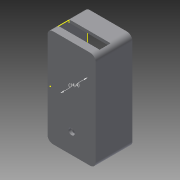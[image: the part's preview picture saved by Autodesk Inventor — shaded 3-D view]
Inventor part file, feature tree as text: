
AUTODESK INVENTOR PART (.ipt)
format: ipt  version: 2014 (Build 180170000, 170)  size: 256,512 bytes
history: native  units: mm
features: sketch x11, extrude x10, projected_geometry x3, fillet x2, chamfer x1
ambient origin geometry x8: Origin, YZ Plane, XZ Plane, XY Plane, X Axis, Y Axis, Z Axis, Center Point
bodies: Solid1 (feature_tree)
feature tree (27):
  extrude  "Extrusion1"  Depth=50.0mm
  extrude  "Extrusion2"  Depth=1.6mm
  extrude  "Extrusion3"  Depth=1.6mm TaperAngle=0.0deg
  extrude  "Extrusion4"  Depth=32.0mm
  extrude  "Extrusion5"  Depth=4.0mm
  fillet  "Fillet1"  Radius=4.0mm
  extrude  "Extrusion6"  Depth=4.0mm
  extrude  "Extrusion7"  Depth=1.2mm
  fillet  "Fillet2"  Radius=1.2mm
  sketch  "Sketch8"  dims[d22=3.5mm d23=3.5mm]
  extrude  "Extrusion8"  Depth=3.5mm
  extrude  "Extrusion9"  Depth=4.0mm
  chamfer  "Chamfer2"  Distance=3.0mm
  extrude  "Extrusion10"  Depth=2.0mm
  sketch  "Sketch1"  dims[d0=23.0mm d1=50.0mm]
  sketch  "Sketch2"  dims[d2=1.6mm d3=1.6mm]
  sketch  "Sketch3"  dims[d4=20.0mm d5=0.0mm d6=1.6mm d7=0.0mm]
  sketch  "Sketch4"  dims[d8=21.0mm d9=32.0mm]
  projected_geometry  "Projected Loop1"
  projected_geometry  "Projected Loop2"
  sketch  "Sketch5"  dims[d10=16.0mm d11=2.6mm d14=4.0mm d15=0.0mm]
  sketch  "Sketch6"  dims[d16=6.0mm d17=4.0mm]
  sketch  "Sketch7"  dims[d18=4.0mm d19=0.0mm d20=1.2mm d21=1.2mm]
  projected_geometry  "Projected Loop3"
  sketch  "Sketch9"  dims[d24=4.0mm d25=0.0mm d26=3.5mm]
  sketch  "Sketch10"  dims[d27=3.5mm]
  sketch  "Sketch11"  dims[d29=7.0mm d30=3.0mm d31=5.2mm d32=4.0mm d33=0.0mm d34=8.0mm d35=2.0mm d36=0.0mm d37=3.0mm d38=14.4mm d39=1.4mm d40=2.0mm d41=0.0mm d45=2.4mm d46=3.143374mm d47=3.143374mm d48=2.4mm d49=3.143374mm d50=3.143374mm d51=2.0mm d52=0.0mm d53=1.0mm d54=2.0mm d55=45.0deg d56=3.4mm d57=2.0mm d58=0.0mm]
